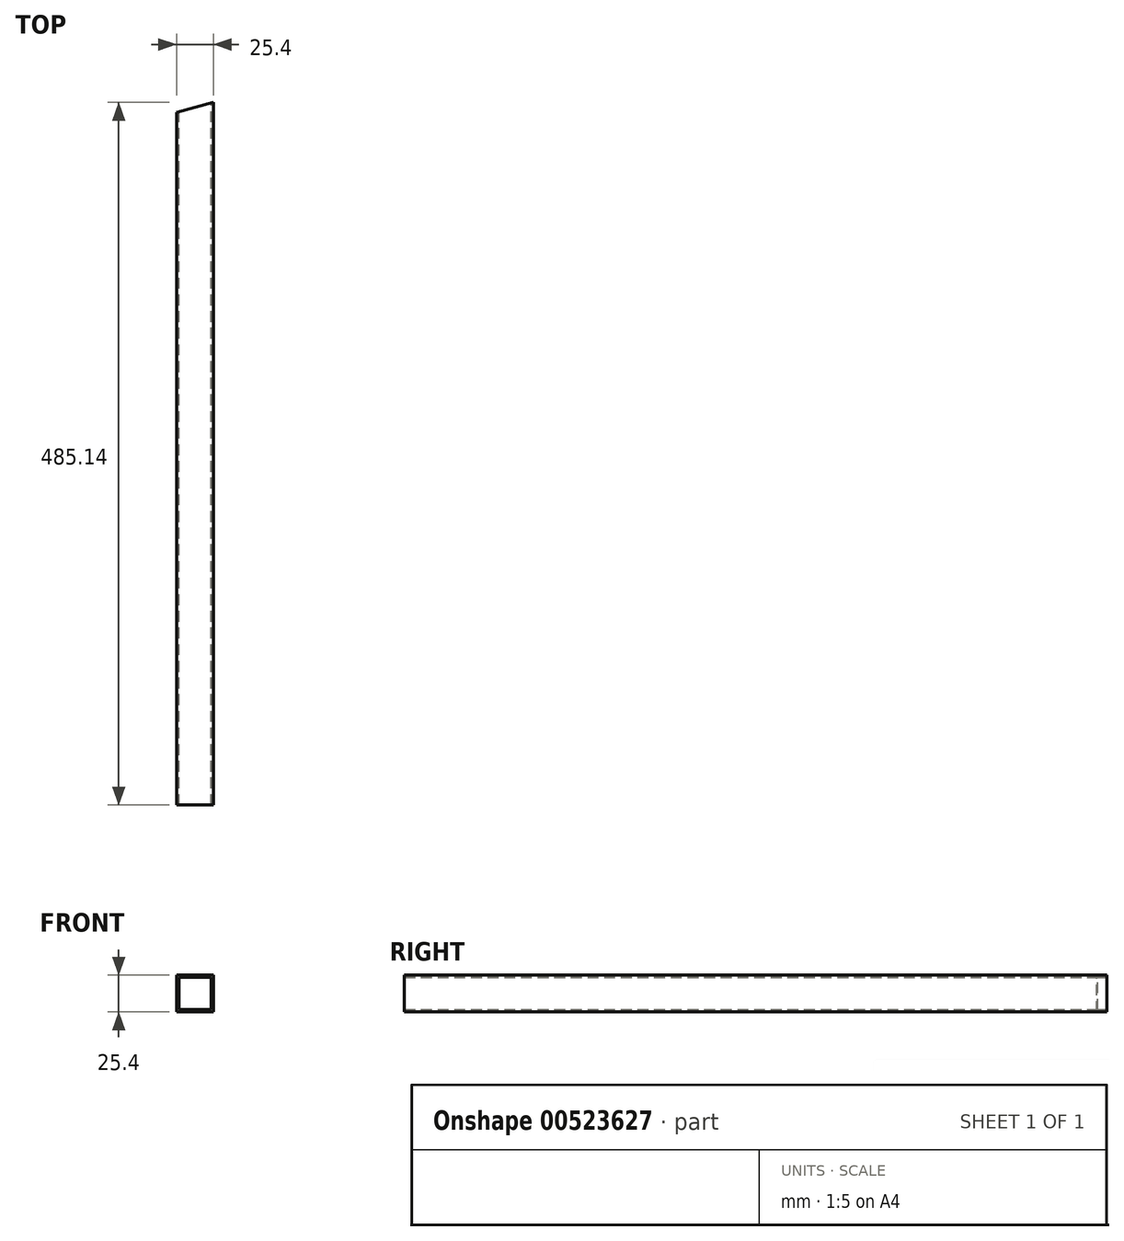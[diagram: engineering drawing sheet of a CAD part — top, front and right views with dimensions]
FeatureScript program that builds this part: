
annotation { "Feature Type Name" : "Feature", "Feature Type Description" : "" }
export const myFeature = defineFeature(function(context is Context, id is Id, definition is map)
    precondition{}
    {
        {
            var Q0;
            Q0=qCreatedBy(makeId("Front.planeOp"),FACE);
            var sketch = newSketch(context, id + "F0", { "sketchPlane" : qUnion([Q0])});
            skLineSegment(sketch, "E0.bottom", {"start": v(-12.7, -12.7) * mm, "end": v(12.7, -12.7) * mm});
            skLineSegment(sketch, "E0.top", {"start": v(-12.7, 12.7) * mm, "end": v(12.7, 12.7) * mm});
            skLineSegment(sketch, "E0.left", {"start": v(-12.7, -12.7) * mm, "end": v(-12.7, 12.7) * mm});
            skLineSegment(sketch, "E0.right", {"start": v(12.7, -12.7) * mm, "end": v(12.7, 12.7) * mm});
            skLineSegment(sketch, "E1.bottom", {"start": v(-11.11, -11.11) * mm, "end": v(11.11, -11.11) * mm});
            skLineSegment(sketch, "E1.top", {"start": v(-11.11, 11.11) * mm, "end": v(11.11, 11.11) * mm});
            skLineSegment(sketch, "E1.left", {"start": v(-11.11, -11.11) * mm, "end": v(-11.11, 11.11) * mm});
            skLineSegment(sketch, "E1.right", {"start": v(11.11, -11.11) * mm, "end": v(11.11, 11.11) * mm});
            skLineSegment(sketch, "E2", {"start": v(-11.11, 0) * mm, "end": v(11.11, 0) * mm, "construction": true});
            skLineSegment(sketch, "E3", {"start": v(0, 12.7) * mm, "end": v(0, -12.7) * mm, "construction": true});
            skSolve(sketch);
        }
        {
            var Q0;
            Q0=qSketchRegion(id+"F0",true);
            extrude(context, id + "F1", {"entities" : qUnion([Q0]), "endBound" : BoundingType.SYMMETRIC, "depth" : 485.14 * mm, "offsetDistance" : 25.4 * mm});
        }
        {
            var Q0;
            Q0=makeQuery(id+"F1.opExtrude","SWEPT_FACE",FACE,{"disambiguationData":[OSD([sQuery(id+"F0.wireOp",EDGE,"E0.top")])]});
            var sketch = newSketch(context, id + "F2", { "sketchPlane" : qUnion([Q0])});
            skLineSegment(sketch, "E4", {"start": v(-12.7, 242.57) * mm, "end": v(-12.7, 235.62) * mm});
            skLineSegment(sketch, "E5", {"start": v(-12.7, 235.62) * mm, "end": v(12.7, 242.57) * mm});
            skLineSegment(sketch, "E6", {"start": v(12.7, 242.57) * mm, "end": v(-12.7, 242.57) * mm});
            skSolve(sketch);
        }
        {
            var Q0;
            Q0 = qSketchRegion(id + "F2", true);
            extrude(context, id + "F3", {"entities" : qUnion([Q0]), "operationType" : NewBodyOperationType.REMOVE, "endBound" : BoundingType.THROUGH_ALL, "oppositeDirection" : true, "depth" : 25.4 * mm, "offsetDistance" : 25.4 * mm});
        }
    });
